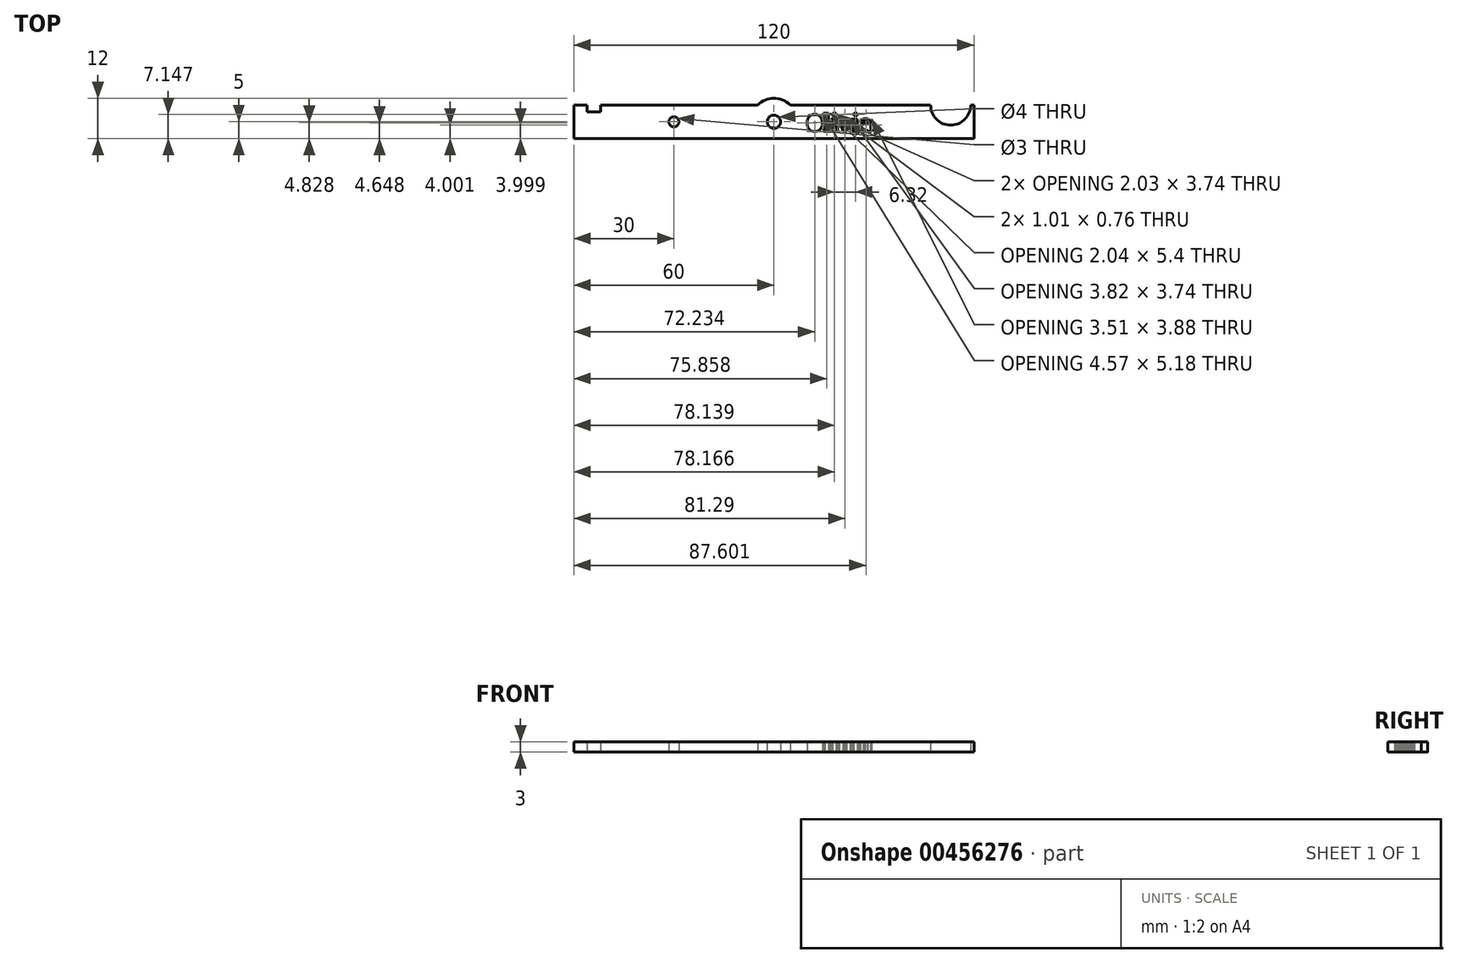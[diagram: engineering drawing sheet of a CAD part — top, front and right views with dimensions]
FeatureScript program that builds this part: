
annotation { "Feature Type Name" : "Feature", "Feature Type Description" : "" }
export const myFeature = defineFeature(function(context is Context, id is Id, definition is map)
    precondition{}
    {
        {
            var Q0;
            Q0=qCreatedBy(makeId("Top.planeOp"),FACE);
            var sketch = newSketch(context, id + "F0", { "sketchPlane" : qUnion([Q0])});
            skLineSegment(sketch, "E0.bottom", {"start": v(-60, 5) * mm, "end": v(60, 5) * mm});
            skLineSegment(sketch, "E0.top", {"start": v(-60, -5) * mm, "end": v(60, -5) * mm});
            skLineSegment(sketch, "E0.left", {"start": v(-60, 5) * mm, "end": v(-60, -5) * mm});
            skLineSegment(sketch, "E0.right", {"start": v(60, 5) * mm, "end": v(60, -5) * mm});
            skPoint(sketch, "E0.middle", {"position": v(0, 0) * mm});
            skLineSegment(sketch, "E1.bottom", {"start": v(-56, 5) * mm, "end": v(-52, 5) * mm});
            skLineSegment(sketch, "E1.top", {"start": v(-56, 3) * mm, "end": v(-52, 3) * mm});
            skLineSegment(sketch, "E1.left", {"start": v(-56, 5) * mm, "end": v(-56, 3) * mm});
            skLineSegment(sketch, "E1.right", {"start": v(-52, 5) * mm, "end": v(-52, 3) * mm});
            skCircle(sketch, "E2", {"center": v(0, 0) * mm, "radius": 2 * mm});
            skCircle(sketch, "E3", {"center": v(0, 0) * mm, "radius": 7 * mm});
            skCircle(sketch, "E4", {"center": v(-30, 0) * mm, "radius": 1.5 * mm});
            skCircle(sketch, "E5", {"center": v(53, 5) * mm, "radius": 6 * mm});
            skText(sketch, "E6", { "text": "Olivia", "fontName": "RobotoSlab-Bold.ttf"});
            const initialGuessF0  = {"E6": [0.00972, -0.00287, 1, 0, 0.0051]};
            skSetInitialGuess(sketch, initialGuessF0);
            skSolve(sketch);
        }
        {
            var Q0;
            {var subQ0=sQuery(id+"F0.wireOp",EDGE,"E0.left");Q0=makeQuery(id+"F0.imprint","IMPRINT",FACE,{"disambiguationData":[TD([[makeQuery(id+"F0.imprint","IMPRINT",EDGE,{"derivedFrom":subQ0}),1.0]])]});}
            var Q1;
            Q1=makeQuery(id+"F0.imprint","IMPRINT",FACE,{"disambiguationData":[TD([[makeQuery(id+"F0.imprint","IMPRINT",EDGE,{"derivedFrom":sQuery(id+"F0.wireOp",EDGE,"E2")}),-1.0]])]});
            var Q2;
            {var subQ0=sQuery(id+"F0.wireOp",EDGE,"E3");var subQ1=sQuery(id+"F0.wireOp",EDGE,"E0.top");var subQ2=makeQuery(id+"F0.imprint","INTERSECT",VERTEX,{"disambiguationData":[OD(0.0)],"derivedFrom":[subQ1,subQ0]});Q2=makeQuery(id+"F0.imprint","IMPRINT",FACE,{"disambiguationData":[TD([[makeQuery(id+"F0.imprint","IMPRINT",EDGE,{"disambiguationData":[TD([[subQ2,-1.0]])],"derivedFrom":subQ1}),-1.0]])]});}
            var Q3;
            {var subQ0=sQuery(id+"F0.wireOp",EDGE,"E0.right");Q3=makeQuery(id+"F0.imprint","IMPRINT",FACE,{"disambiguationData":[TD([[makeQuery(id+"F0.imprint","IMPRINT",EDGE,{"derivedFrom":subQ0}),-1.0]])]});}
            var Q4;
            {var subQ0=sQuery(id+"F0.wireOp",EDGE,"E3");var subQ1=sQuery(id+"F0.wireOp",EDGE,"E0.bottom");var subQ2=makeQuery(id+"F0.imprint","INTERSECT",VERTEX,{"disambiguationData":[OD(0.0)],"derivedFrom":[subQ1,subQ0]});Q4=makeQuery(id+"F0.imprint","IMPRINT",FACE,{"disambiguationData":[TD([[makeQuery(id+"F0.imprint","IMPRINT",EDGE,{"disambiguationData":[TD([[subQ2,-1.0]])],"derivedFrom":subQ1}),1.0]])]});}
            extrude(context, id + "F1", {"entities" : qUnion([Q0, Q1, Q2, Q3, Q4]), "depth" : 3 * mm});
        }
    });
